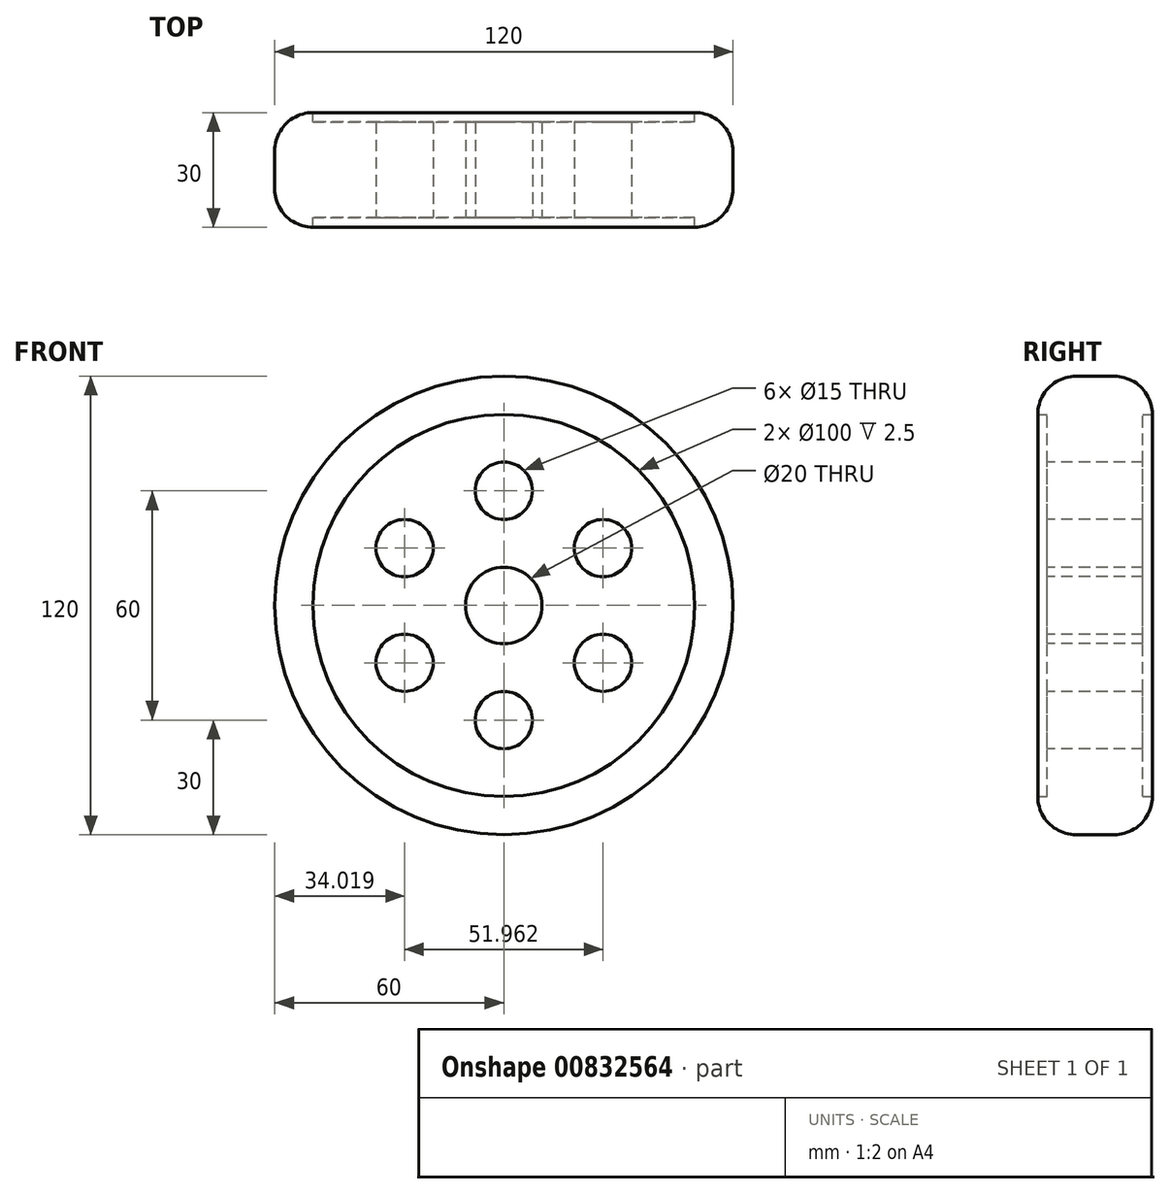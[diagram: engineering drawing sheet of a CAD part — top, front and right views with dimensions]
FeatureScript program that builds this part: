
annotation { "Feature Type Name" : "Feature", "Feature Type Description" : "" }
export const myFeature = defineFeature(function(context is Context, id is Id, definition is map)
    precondition{}
    {
        {
            var Q0;
            Q0=qCreatedBy(makeId("Front.planeOp"),FACE);
            var sketch = newSketch(context, id + "F0", { "sketchPlane" : qUnion([Q0])});
            skCircle(sketch, "E0", {"center": v(0, 0) * mm, "radius": 60 * mm});
            skCircle(sketch, "E1", {"center": v(0, 0) * mm, "radius": 50 * mm});
            skSolve(sketch);
        }
        {
            var Q0;
            Q0=makeQuery(id+"F0.imprint","IMPRINT",FACE,{"disambiguationData":[TD([[makeQuery(id+"F0.imprint","IMPRINT",EDGE,{"derivedFrom":sQuery(id+"F0.wireOp",EDGE,"E0")}),1.0]])]});
            extrude(context, id + "F1", {"entities" : qUnion([Q0]), "endBound" : BoundingType.SYMMETRIC, "depth" : 30 * mm, "offsetDistance" : 25 * mm});
        }
        {
            var Q0;
            Q0=makeQuery(id+"F0.imprint","IMPRINT",FACE,{"disambiguationData":[TD([[makeQuery(id+"F0.imprint","IMPRINT",EDGE,{"derivedFrom":sQuery(id+"F0.wireOp",EDGE,"E1")}),1.0]])]});
            extrude(context, id + "F2", {"entities" : qUnion([Q0]), "operationType" : NewBodyOperationType.ADD, "endBound" : BoundingType.SYMMETRIC, "depth" : 25 * mm, "offsetDistance" : 25 * mm});
        }
        {
            var Q0;
            Q0=makeQuery(id+"F1.opExtrude","CAP_EDGE",EDGE,{"disambiguationData":[OSD([sQuery(id+"F0.wireOp",EDGE,"E0")])],"isStart":false});
            var Q1;
            Q1=makeQuery(id+"F1.opExtrude","CAP_EDGE",EDGE,{"disambiguationData":[OSD([sQuery(id+"F0.wireOp",EDGE,"E0")])],"isStart":true});
            fillet(context, id + "F3", {"entities" : qUnion([Q0, Q1]), "radius" : 10 * mm, "tangentPropagation" : true, "allowEdgeOverflow" : false});
        }
        {
            var Q0;
            Q0=makeQuery(id+"F2.opExtrude","CAP_FACE",FACE,{"disambiguationData":[OSD([sQuery(id+"F0.wireOp",EDGE,"E1")])],"isStart":false});
            var sketch = newSketch(context, id + "F4", { "sketchPlane" : qUnion([Q0])});
            skCircle(sketch, "E2", {"center": v(0, 30) * mm, "radius": 7.5 * mm});
            skCircle(sketch, "E3.1.0", {"center": v(-25.98, 15) * mm, "radius": 7.5 * mm});
            skCircle(sketch, "E3.2.0", {"center": v(-25.98, -15) * mm, "radius": 7.5 * mm});
            skCircle(sketch, "E3.3.0", {"center": v(0, -30) * mm, "radius": 7.5 * mm});
            skCircle(sketch, "E3.4.0", {"center": v(25.98, -15) * mm, "radius": 7.5 * mm});
            skCircle(sketch, "E3.5.0", {"center": v(25.98, 15) * mm, "radius": 7.5 * mm});
            skPoint(sketch, "E3.center", {"position": v(0, 0) * mm});
            skCircle(sketch, "E4", {"center": v(0, 0) * mm, "radius": 10 * mm});
            skSolve(sketch);
        }
        {
            var Q0;
            Q0=makeQuery(id+"F4.imprint","IMPRINT",FACE,{"disambiguationData":[TD([[makeQuery(id+"F4.imprint","IMPRINT",EDGE,{"derivedFrom":sQuery(id+"F4.wireOp",EDGE,"E2")}),1.0]])]});
            var Q1;
            Q1=makeQuery(id+"F4.imprint","IMPRINT",FACE,{"disambiguationData":[TD([[makeQuery(id+"F4.imprint","IMPRINT",EDGE,{"derivedFrom":sQuery(id+"F4.wireOp",EDGE,"E3.1.0")}),1.0]])]});
            var Q2;
            Q2=makeQuery(id+"F4.imprint","IMPRINT",FACE,{"disambiguationData":[TD([[makeQuery(id+"F4.imprint","IMPRINT",EDGE,{"derivedFrom":sQuery(id+"F4.wireOp",EDGE,"E3.2.0")}),1.0]])]});
            var Q3;
            Q3=makeQuery(id+"F4.imprint","IMPRINT",FACE,{"disambiguationData":[TD([[makeQuery(id+"F4.imprint","IMPRINT",EDGE,{"derivedFrom":sQuery(id+"F4.wireOp",EDGE,"E3.3.0")}),1.0]])]});
            var Q4;
            Q4=makeQuery(id+"F4.imprint","IMPRINT",FACE,{"disambiguationData":[TD([[makeQuery(id+"F4.imprint","IMPRINT",EDGE,{"derivedFrom":sQuery(id+"F4.wireOp",EDGE,"E3.4.0")}),1.0]])]});
            var Q5;
            Q5=makeQuery(id+"F4.imprint","IMPRINT",FACE,{"disambiguationData":[TD([[makeQuery(id+"F4.imprint","IMPRINT",EDGE,{"derivedFrom":sQuery(id+"F4.wireOp",EDGE,"E3.5.0")}),1.0]])]});
            extrude(context, id + "F5", {"entities" : qUnion([Q0, Q1, Q2, Q3, Q4, Q5]), "operationType" : NewBodyOperationType.REMOVE, "endBound" : BoundingType.UP_TO_NEXT, "oppositeDirection" : true, "depth" : 25 * mm, "offsetDistance" : 25 * mm});
        }
        {
            var Q0;
            Q0=makeQuery(id+"F4.imprint","IMPRINT",FACE,{"disambiguationData":[TD([[makeQuery(id+"F4.imprint","IMPRINT",EDGE,{"derivedFrom":sQuery(id+"F4.wireOp",EDGE,"E4")}),1.0]])]});
            extrude(context, id + "F6", {"entities" : qUnion([Q0]), "operationType" : NewBodyOperationType.REMOVE, "endBound" : BoundingType.UP_TO_NEXT, "oppositeDirection" : true, "depth" : 25 * mm, "offsetDistance" : 25 * mm});
        }
    });
